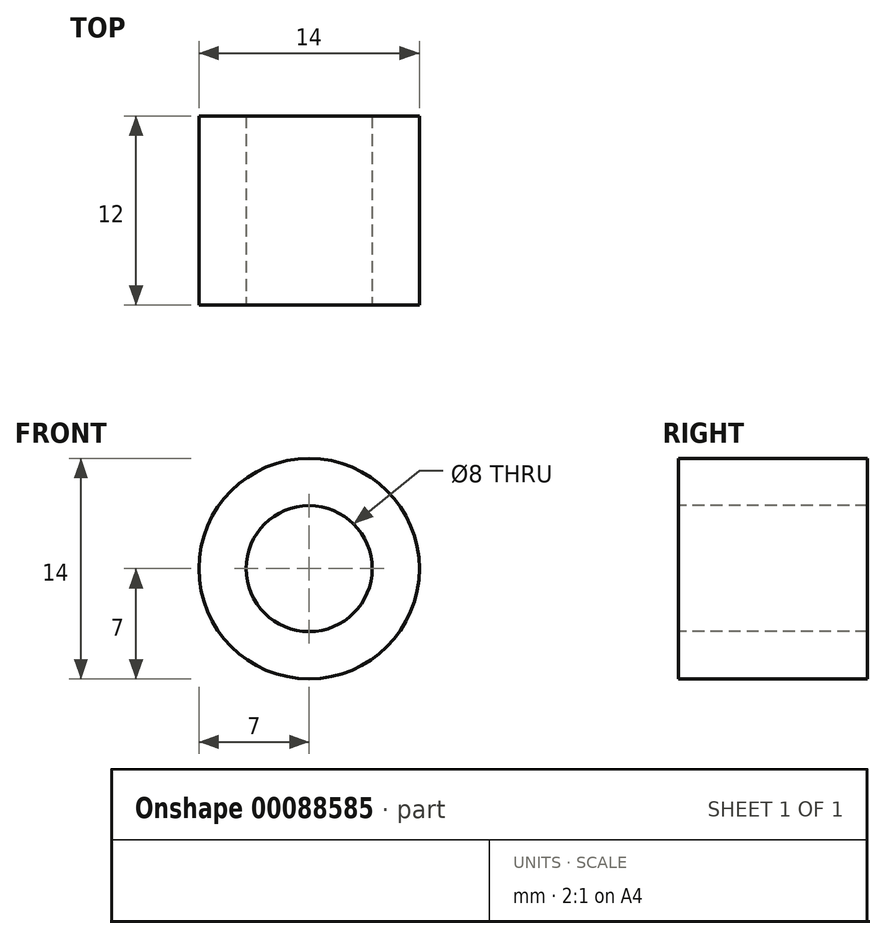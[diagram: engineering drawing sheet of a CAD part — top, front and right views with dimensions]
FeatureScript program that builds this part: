
annotation { "Feature Type Name" : "Feature", "Feature Type Description" : "" }
export const myFeature = defineFeature(function(context is Context, id is Id, definition is map)
    precondition{}
    {
        {
            var Q0;
            Q0=qCreatedBy(makeId("Front.planeOp"),FACE);
            var sketch = newSketch(context, id + "F0", { "sketchPlane" : qUnion([Q0])});
            skCircle(sketch, "E0", {"center": v(0, 0) * mm, "radius": 7 * mm});
            skCircle(sketch, "E1", {"center": v(0, 0) * mm, "radius": 4 * mm});
            skSolve(sketch);
        }
        {
            var Q0;
            Q0=makeQuery(id+"F0.imprint","IMPRINT",FACE,{"disambiguationData":[TD([[makeQuery(id+"F0.imprint","IMPRINT",EDGE,{"derivedFrom":sQuery(id+"F0.wireOp",EDGE,"E0")}),1.0]])]});
            extrude(context, id + "F1", {"entities" : qUnion([Q0]), "oppositeDirection" : true, "depth" : 12 * mm});
        }
    });
